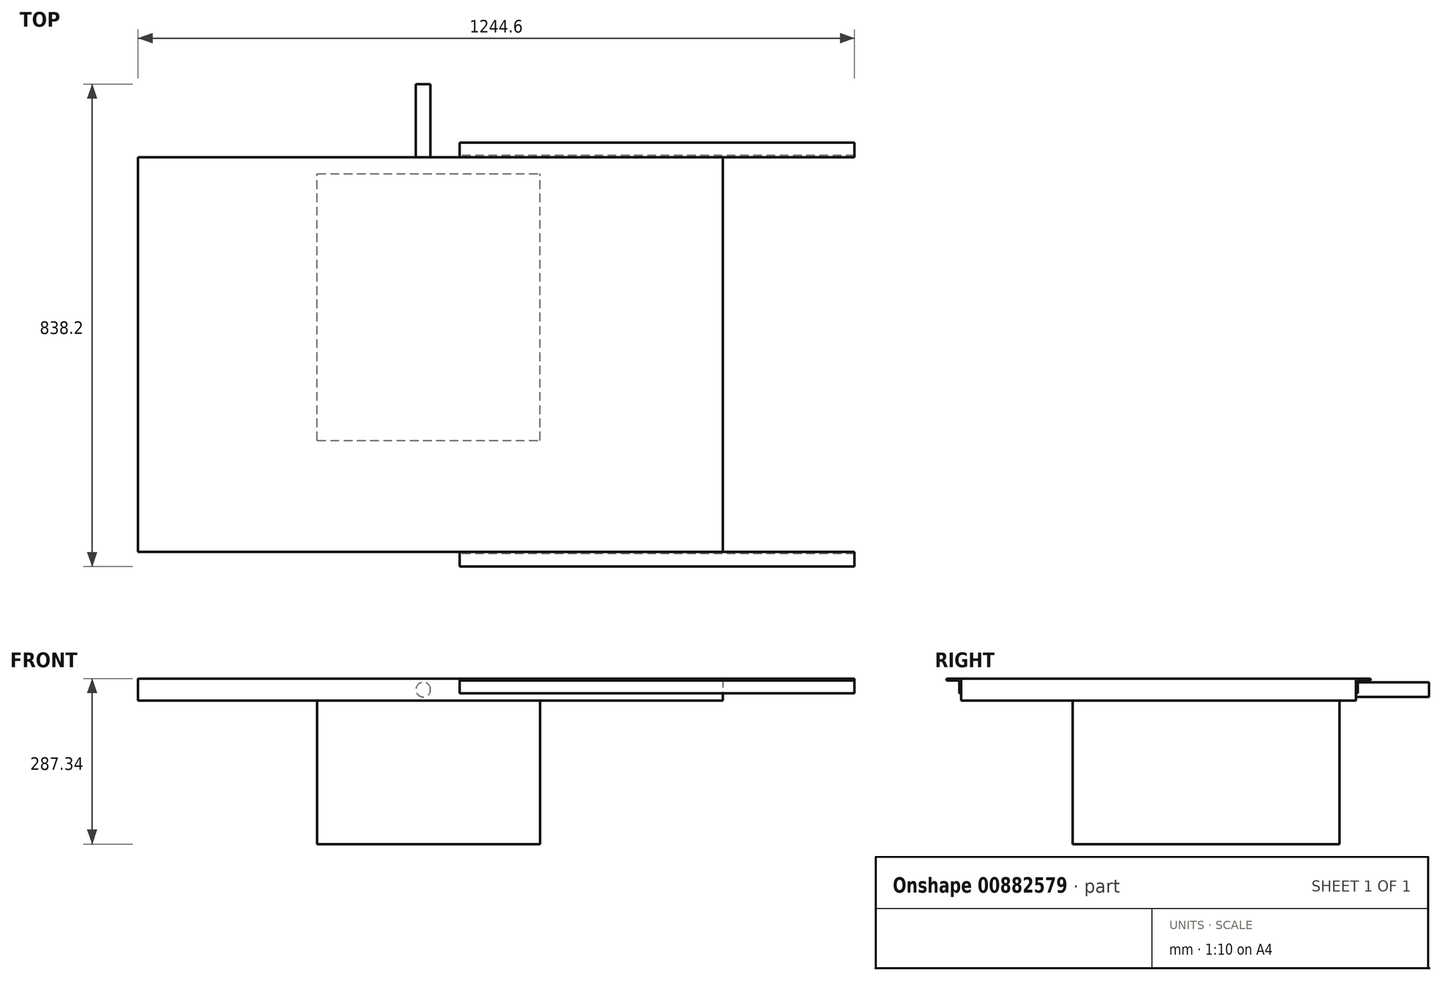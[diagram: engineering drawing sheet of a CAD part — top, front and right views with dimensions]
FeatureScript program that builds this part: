
annotation { "Feature Type Name" : "Feature", "Feature Type Description" : "" }
export const myFeature = defineFeature(function(context is Context, id is Id, definition is map)
    precondition{}
    {
        {
            var Q0;
            Q0=qCreatedBy(makeId("Top.planeOp"),FACE);
            var sketch = newSketch(context, id + "F0", { "sketchPlane" : qUnion([Q0])});
            skLineSegment(sketch, "E0.bottom", {"start": v(0, 0) * mm, "end": v(1016, 0) * mm});
            skLineSegment(sketch, "E0.top", {"start": v(0, -685.8) * mm, "end": v(1016, -685.8) * mm});
            skLineSegment(sketch, "E0.left", {"start": v(0, 0) * mm, "end": v(0, -685.8) * mm});
            skLineSegment(sketch, "E0.right", {"start": v(1016, 0) * mm, "end": v(1016, -685.8) * mm});
            skSolve(sketch);
        }
        {
            var Q0;
            Q0=makeQuery(id+"F0.imprint","IMPRINT",FACE,{"disambiguationData":[TD([[makeQuery(id+"F0.imprint","IMPRINT",EDGE,{"derivedFrom":sQuery(id+"F0.wireOp",EDGE,"E0.bottom")}),-1.0]])]});
            extrude(context, id + "F1", {"entities" : qUnion([Q0]), "depth" : 38.1 * mm, "offsetDistance" : 25.4 * mm});
        }
        {
            var Q0;
            Q0=makeQuery(id+"F1.opExtrude","CAP_FACE",FACE,{"disambiguationData":[OSD([sQuery(id+"F0.wireOp",EDGE,"E0.bottom"),sQuery(id+"F0.wireOp",EDGE,"E0.top"),sQuery(id+"F0.wireOp",EDGE,"E0.left"),sQuery(id+"F0.wireOp",EDGE,"E0.right")])],"isStart":true});
            var sketch = newSketch(context, id + "F2", { "sketchPlane" : qUnion([Q0])});
            skLineSegment(sketch, "E1.bottom", {"start": v(311.15, 492.12) * mm, "end": v(698.5, 492.13) * mm});
            skLineSegment(sketch, "E1.top", {"start": v(311.15, 28.57) * mm, "end": v(698.5, 28.58) * mm});
            skLineSegment(sketch, "E1.left", {"start": v(311.15, 492.12) * mm, "end": v(311.15, 28.57) * mm});
            skLineSegment(sketch, "E1.right", {"start": v(698.5, 492.13) * mm, "end": v(698.5, 28.58) * mm});
            skSolve(sketch);
        }
        {
            var Q0;
            Q0=makeQuery(id+"F2.imprint","IMPRINT",FACE,{"disambiguationData":[TD([[makeQuery(id+"F2.imprint","IMPRINT",EDGE,{"derivedFrom":sQuery(id+"F2.wireOp",EDGE,"E1.bottom")}),-1.0]])]});
            extrude(context, id + "F3", {"entities" : qUnion([Q0]), "operationType" : NewBodyOperationType.ADD, "depth" : 249.24 * mm, "offsetDistance" : 25.4 * mm});
        }
        {
            var Q0;
            Q0=makeQuery(id+"F1.opExtrude","SWEPT_FACE",FACE,{"disambiguationData":[OSD([sQuery(id+"F0.wireOp",EDGE,"E0.bottom")])]});
            var sketch = newSketch(context, id + "F4", { "sketchPlane" : qUnion([Q0])});
            skCircle(sketch, "E2", {"center": v(-495.3, 19.05) * mm, "radius": 12.7 * mm});
            skSolve(sketch);
        }
        {
            var Q0;
            Q0 = qSketchRegion(id + "F4", true);
            extrude(context, id + "F5", {"entities" : qUnion([Q0]), "operationType" : NewBodyOperationType.ADD, "depth" : 127 * mm, "offsetDistance" : 25.4 * mm});
        }
        {
            var Q0;
            Q0=makeQuery(id+"F1.opExtrude","SWEPT_FACE",FACE,{"disambiguationData":[OSD([sQuery(id+"F0.wireOp",EDGE,"E0.right")])]});
            var sketch = newSketch(context, id + "F6", { "sketchPlane" : qUnion([Q0])});
            skLineSegment(sketch, "E3", {"start": v(-685.8, 38.1) * mm, "end": v(-711.2, 38.1) * mm});
            skLineSegment(sketch, "E4", {"start": v(-711.2, 38.1) * mm, "end": v(-711.2, 34.93) * mm});
            skLineSegment(sketch, "E5", {"start": v(-711.2, 34.93) * mm, "end": v(-688.98, 34.93) * mm});
            skLineSegment(sketch, "E6", {"start": v(-688.98, 34.93) * mm, "end": v(-688.98, 12.7) * mm});
            skLineSegment(sketch, "E7", {"start": v(-688.98, 12.7) * mm, "end": v(-685.8, 12.7) * mm});
            skLineSegment(sketch, "E8", {"start": v(-685.8, 12.7) * mm, "end": v(-685.8, 38.1) * mm});
            skLineSegment(sketch, "E9", {"start": v(0, 38.1) * mm, "end": v(25.4, 38.1) * mm});
            skLineSegment(sketch, "E10", {"start": v(25.4, 38.1) * mm, "end": v(25.4, 34.93) * mm});
            skLineSegment(sketch, "E11", {"start": v(25.4, 34.93) * mm, "end": v(3.17, 34.93) * mm});
            skLineSegment(sketch, "E12", {"start": v(3.17, 34.92) * mm, "end": v(3.17, 12.7) * mm});
            skLineSegment(sketch, "E13", {"start": v(3.17, 12.7) * mm, "end": v(0, 12.7) * mm});
            skLineSegment(sketch, "E14", {"start": v(0, 12.7) * mm, "end": v(0, 38.1) * mm});
            skSolve(sketch);
        }
        {
            var Q0;
            Q0 = qSketchRegion(id + "F6", true);
            extrude(context, id + "F7", {"entities" : qUnion([Q0]), "depth" : 228.6 * mm, "offsetDistance" : 25.4 * mm, "hasSecondDirection" : true, "secondDirectionOppositeDirection" : true, "secondDirectionDepth" : 457.2 * mm});
        }
    });
